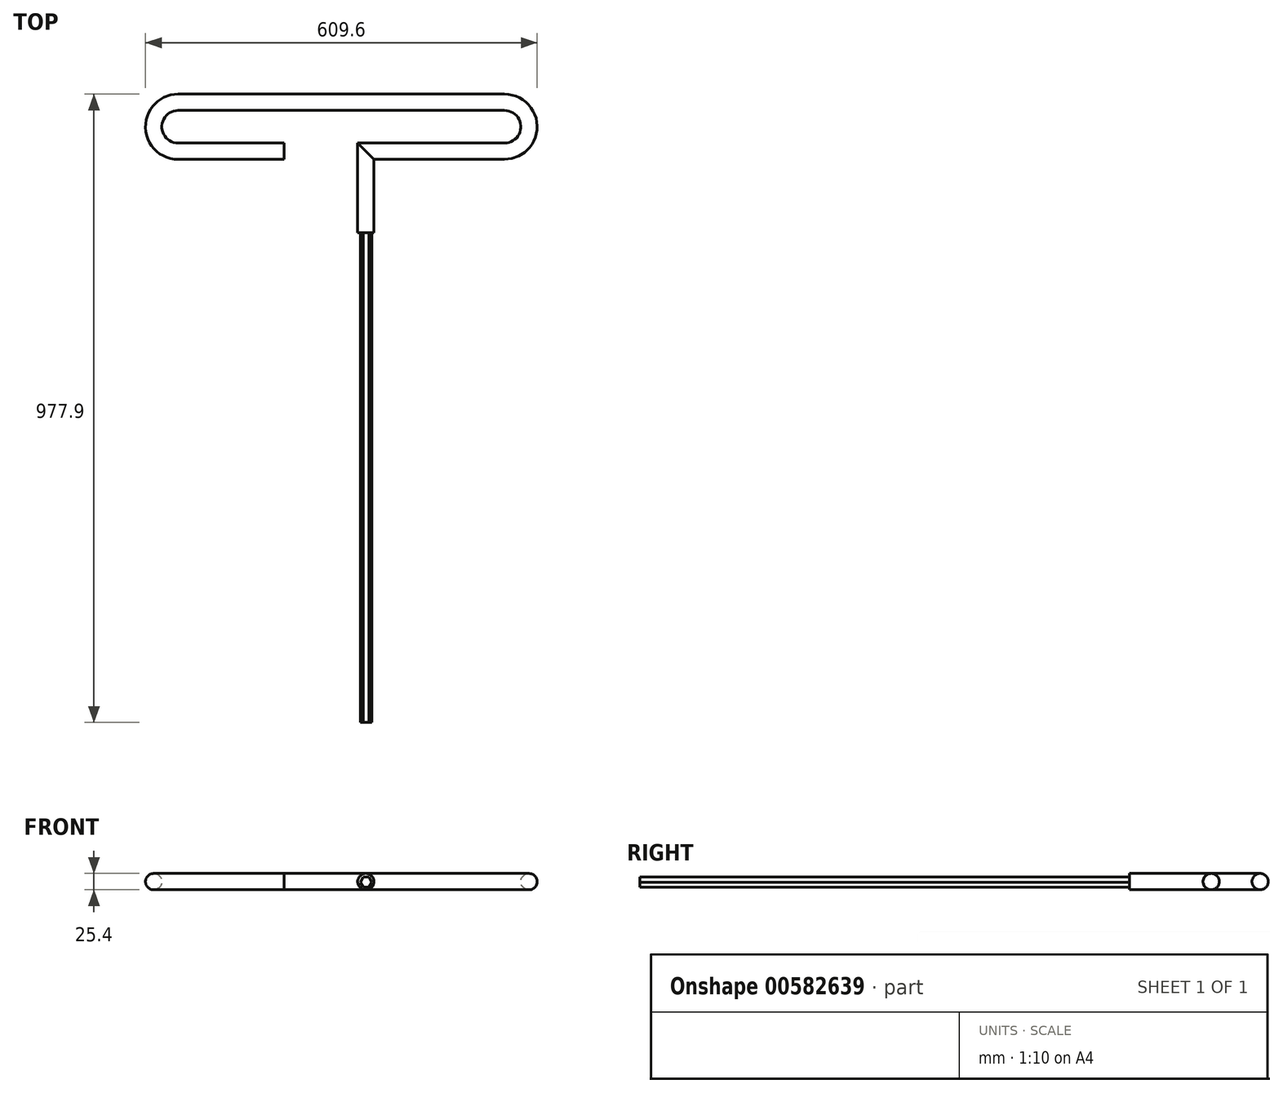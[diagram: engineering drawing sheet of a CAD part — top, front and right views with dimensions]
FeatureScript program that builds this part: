
annotation { "Feature Type Name" : "Feature", "Feature Type Description" : "" }
export const myFeature = defineFeature(function(context is Context, id is Id, definition is map)
    precondition{}
    {
        {
            var Q0;
            Q0=qCreatedBy(makeId("Front.planeOp"),FACE);
            var sketch = newSketch(context, id + "F0", { "sketchPlane" : qUnion([Q0])});
            skCircle(sketch, "E0", {"center": v(0, 0) * mm, "radius": 12.7 * mm});
            skSolve(sketch);
        }
        {
            var Q0;
            Q0=qCreatedBy(makeId("Top.planeOp"),FACE);
            var sketch = newSketch(context, id + "F1", { "sketchPlane" : qUnion([Q0])});
            skLineSegment(sketch, "E1", {"start": v(0, 0) * mm, "end": v(0, 127) * mm});
            skLineSegment(sketch, "E2", {"start": v(0, 127) * mm, "end": v(215.9, 127) * mm});
            skLineSegment(sketch, "E3", {"start": v(254, 165.1) * mm, "end": v(254, 165.1) * mm});
            skLineSegment(sketch, "E4", {"start": v(215.9, 203.2) * mm, "end": v(-292.1, 203.2) * mm});
            skLineSegment(sketch, "E5", {"start": v(-330.2, 165.1) * mm, "end": v(-330.2, 165.1) * mm});
            skLineSegment(sketch, "E6", {"start": v(-127, 127) * mm, "end": v(-292.1, 127) * mm});
            skPoint(sketch, "E7.visualSharp", {"position": v(-330.2, 127) * mm});
            skArc(sketch, "E7.filletArc", {"start": v(-330.2, 165.1) * mm, "mid": v(-319.04, 138.16) * mm, "end": v(-292.1, 127) * mm});
            skPoint(sketch, "E8.visualSharp", {"position": v(-330.2, 203.2) * mm});
            skArc(sketch, "E8.filletArc", {"start": v(-292.1, 203.2) * mm, "mid": v(-319.04, 192.04) * mm, "end": v(-330.2, 165.1) * mm});
            skPoint(sketch, "E9.visualSharp", {"position": v(254, 203.2) * mm});
            skArc(sketch, "E9.filletArc", {"start": v(254, 165.1) * mm, "mid": v(242.84, 192.04) * mm, "end": v(215.9, 203.2) * mm});
            skPoint(sketch, "E10.visualSharp", {"position": v(254, 127) * mm});
            skArc(sketch, "E10.filletArc", {"start": v(215.9, 127) * mm, "mid": v(242.84, 138.16) * mm, "end": v(254, 165.1) * mm});
            skSolve(sketch);
        }
        {
            var Q0;
            Q0 = qSketchRegion(id + "F0", true);
            var Q1;
            Q1 = qConstructionFilter(qBodyType(qCreatedBy(id + "F1" ,EDGE), BodyType.WIRE), ConstructionObject.NO);
            sweep(context, id + "F2", {"profiles" : qUnion([Q0]), "path" : qUnion([Q1])});
        }
        {
            var Q0;
            Q0=makeQuery(id+"F0.imprint","IMPRINT",FACE,{"disambiguationData":[TD([[makeQuery(id+"F0.imprint","IMPRINT",EDGE,{"derivedFrom":sQuery(id+"F0.wireOp",EDGE,"E0")}),1.0]])]});
            var sketch = newSketch(context, id + "F3", { "sketchPlane" : qUnion([Q0])});
            skLineSegment(sketch, "E11", {"start": v(-4.2, 6.93) * mm, "end": v(4.7, 6.93) * mm});
            skLineSegment(sketch, "E12", {"start": v(4.7, 6.93) * mm, "end": v(9.14, -0.76) * mm});
            skLineSegment(sketch, "E13", {"start": v(9.14, -0.76) * mm, "end": v(4.7, -8.46) * mm});
            skLineSegment(sketch, "E14", {"start": v(4.7, -8.46) * mm, "end": v(-4.2, -8.46) * mm});
            skLineSegment(sketch, "E15", {"start": v(-4.2, -8.46) * mm, "end": v(-8.64, -0.76) * mm});
            skLineSegment(sketch, "E16", {"start": v(-8.64, -0.76) * mm, "end": v(-4.2, 6.93) * mm});
            skSolve(sketch);
        }
        {
            var Q0;
            Q0 = qSketchRegion(id + "F3", true);
            extrude(context, id + "F4", {"entities" : qUnion([Q0]), "operationType" : NewBodyOperationType.ADD, "depth" : 762 * mm, "offsetDistance" : 25.4 * mm});
        }
    });
